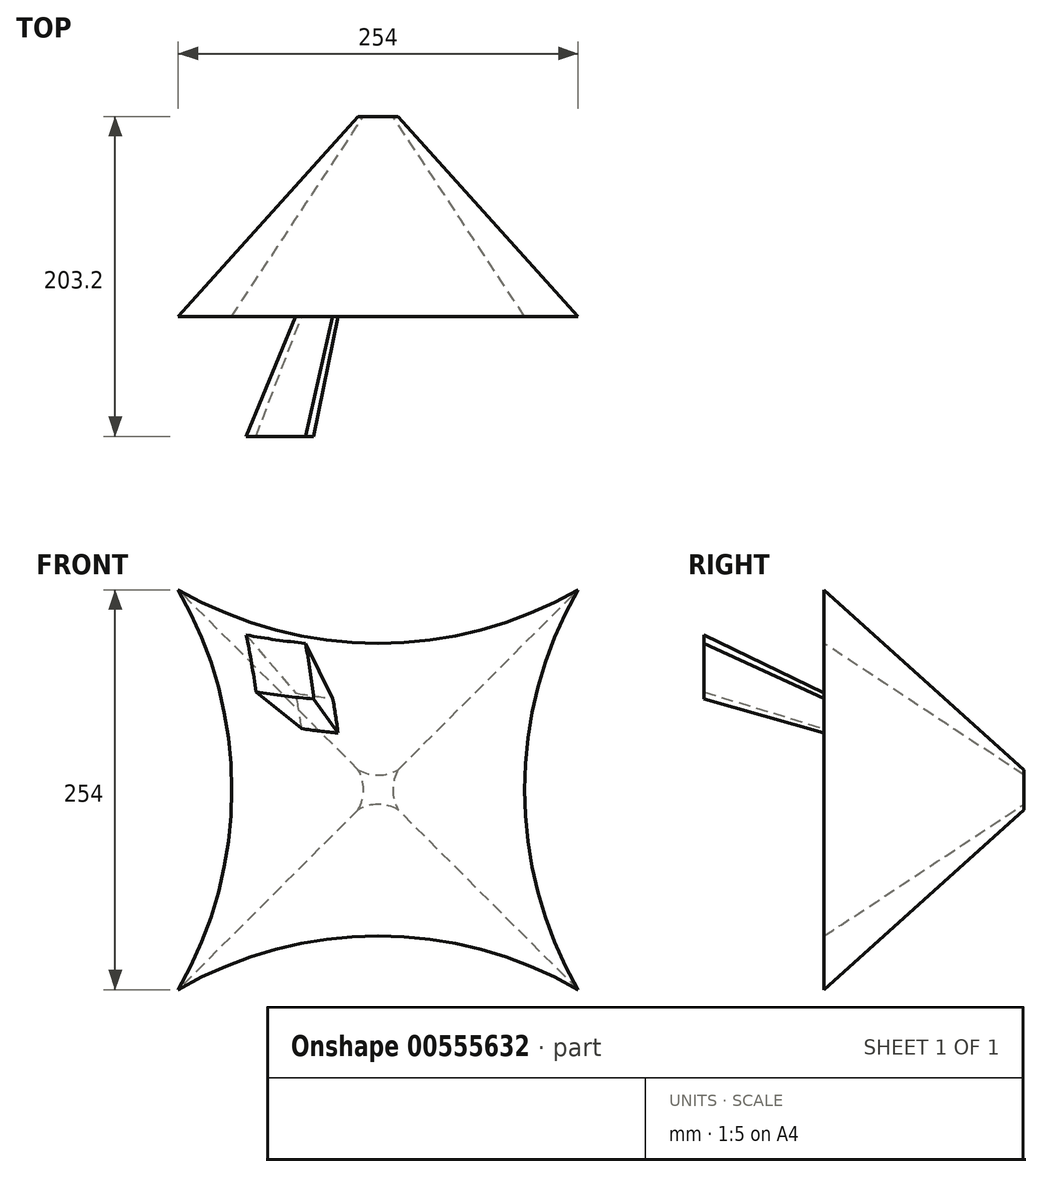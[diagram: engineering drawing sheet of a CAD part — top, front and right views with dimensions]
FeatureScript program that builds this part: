
annotation { "Feature Type Name" : "Feature", "Feature Type Description" : "" }
export const myFeature = defineFeature(function(context is Context, id is Id, definition is map)
    precondition{}
    {
        {
            var Q0;
            Q0=qCreatedBy(makeId("Front.planeOp"),FACE);
            var sketch = newSketch(context, id + "F0", { "sketchPlane" : qUnion([Q0])});
            skLineSegment(sketch, "E0.bottom", {"start": v(12.7, 12.7) * mm, "end": v(-12.7, 12.7) * mm, "construction": true});
            skLineSegment(sketch, "E0.top", {"start": v(12.7, -12.7) * mm, "end": v(-12.7, -12.7) * mm, "construction": true});
            skLineSegment(sketch, "E0.left", {"start": v(12.7, 12.7) * mm, "end": v(12.7, -12.7) * mm, "construction": true});
            skLineSegment(sketch, "E0.right", {"start": v(-12.7, 12.7) * mm, "end": v(-12.7, -12.7) * mm, "construction": true});
            skPoint(sketch, "E0.middle", {"position": v(0, 0) * mm});
            skArc(sketch, "E1", {"start": v(-12.7, 12.7) * mm, "mid": v(0, 9.3) * mm, "end": v(12.7, 12.7) * mm});
            skArc(sketch, "E2", {"start": v(12.7, 12.7) * mm, "mid": v(9.3, 0) * mm, "end": v(12.7, -12.7) * mm});
            skArc(sketch, "E3", {"start": v(12.7, -12.7) * mm, "mid": v(0, -9.3) * mm, "end": v(-12.7, -12.7) * mm});
            skArc(sketch, "E4", {"start": v(-12.7, -12.7) * mm, "mid": v(-9.3, 0) * mm, "end": v(-12.7, 12.7) * mm});
            skArc(sketch, "E5", {"start": v(-6.35, -10.1) * mm, "mid": v(-4.6, 0) * mm, "end": v(-6.35, 10.1) * mm});
            skArc(sketch, "E6", {"start": v(-3.8, 9.58) * mm, "mid": v(-2.36, 0) * mm, "end": v(-3.8, -9.58) * mm});
            skArc(sketch, "E7", {"start": v(-10.47, 7.62) * mm, "mid": v(0, 5.67) * mm, "end": v(10.47, 7.62) * mm});
            skArc(sketch, "E8", {"start": v(-9.81, 5.08) * mm, "mid": v(0, 3.5) * mm, "end": v(9.81, 5.08) * mm});
            skSolve(sketch);
        }
        {
            var Q0;
            {var subQ0=sQuery(id+"F0.wireOp",EDGE,"E3");var subQ1=sQuery(id+"F0.wireOp",EDGE,"E2");var subQ2=makeQuery(id+"F0.imprint","INTERSECT",VERTEX,{"derivedFrom":[subQ1,subQ0]});Q0=makeQuery(id+"F0.imprint","IMPRINT",FACE,{"disambiguationData":[TD([[makeQuery(id+"F0.imprint","IMPRINT",EDGE,{"disambiguationData":[TD([[subQ2,1.0]])],"derivedFrom":subQ1}),-1.0]])]});}
            var sketch = newSketch(context, id + "F1", { "sketchPlane" : qUnion([Q0])});
            skArc(sketch, "E9.0", {"start": v(-12.7, -12.7) * mm, "mid": v(-9.3, 0) * mm, "end": v(-12.7, 12.7) * mm});
            skArc(sketch, "E9.1", {"start": v(12.7, -12.7) * mm, "mid": v(0, -9.3) * mm, "end": v(-12.7, -12.7) * mm});
            skArc(sketch, "E9.2", {"start": v(12.7, 12.7) * mm, "mid": v(9.3, 0) * mm, "end": v(12.7, -12.7) * mm});
            skArc(sketch, "E9.3", {"start": v(-12.7, 12.7) * mm, "mid": v(0, 9.3) * mm, "end": v(12.7, 12.7) * mm});
            skSolve(sketch);
        }
        {
            var Q0;
            Q0=qCreatedBy(makeId("Front.planeOp"),FACE);
            cPlane(context, id + "F2", {"entities" : qUnion([Q0]), "cplaneType" : CPlaneType.OFFSET, "offset" : 127 * mm, "width" : 152.4 * mm, "height" : 152.4 * mm});
        }
        {
            var Q0;
            Q0=qCreatedBy(id+"F2.planeOp",FACE);
            var sketch = newSketch(context, id + "F3", { "sketchPlane" : qUnion([Q0])});
            skLineSegment(sketch, "E10.bottom", {"start": v(127, 127) * mm, "end": v(-127, 127) * mm, "construction": true});
            skLineSegment(sketch, "E10.top", {"start": v(127, -127) * mm, "end": v(-127, -127) * mm, "construction": true});
            skLineSegment(sketch, "E10.left", {"start": v(127, 127) * mm, "end": v(127, -127) * mm, "construction": true});
            skLineSegment(sketch, "E10.right", {"start": v(-127, 127) * mm, "end": v(-127, -127) * mm, "construction": true});
            skPoint(sketch, "E10.middle", {"position": v(0, 0) * mm});
            skArc(sketch, "E11", {"start": v(-127, 127) * mm, "mid": v(0, 92.97) * mm, "end": v(127, 127) * mm});
            skArc(sketch, "E12", {"start": v(127, 127) * mm, "mid": v(92.97, 0) * mm, "end": v(127, -127) * mm});
            skArc(sketch, "E13", {"start": v(127, -127) * mm, "mid": v(0, -92.97) * mm, "end": v(-127, -127) * mm});
            skArc(sketch, "E14", {"start": v(-127, -127) * mm, "mid": v(-92.97, 0) * mm, "end": v(-127, 127) * mm});
            skArc(sketch, "E15", {"start": v(-63.5, -101.04) * mm, "mid": v(-46.03, 0) * mm, "end": v(-63.5, 101.04) * mm});
            skArc(sketch, "E16", {"start": v(-38.1, 95.84) * mm, "mid": v(-23.57, 0) * mm, "end": v(-38.1, -95.84) * mm});
            skArc(sketch, "E17", {"start": v(-104.67, 76.2) * mm, "mid": v(0, 56.67) * mm, "end": v(104.67, 76.2) * mm});
            skArc(sketch, "E18", {"start": v(-98.1, 50.8) * mm, "mid": v(0, 34.98) * mm, "end": v(98.1, 50.8) * mm});
            skSolve(sketch);
        }
        {
            var Q0;
            Q0=qCreatedBy(id+"F2.planeOp",FACE);
            var sketch = newSketch(context, id + "F4", { "sketchPlane" : qUnion([Q0])});
            skArc(sketch, "E19.0", {"start": v(-127, 127) * mm, "mid": v(0, 92.97) * mm, "end": v(127, 127) * mm});
            skArc(sketch, "E19.1", {"start": v(-127, -127) * mm, "mid": v(-92.97, 0) * mm, "end": v(-127, 127) * mm});
            skArc(sketch, "E19.2", {"start": v(127, -127) * mm, "mid": v(0, -92.97) * mm, "end": v(-127, -127) * mm});
            skArc(sketch, "E19.3", {"start": v(127, 127) * mm, "mid": v(92.97, 0) * mm, "end": v(127, -127) * mm});
            skSolve(sketch);
        }
        {
            var Q0;
            Q0=qCreatedBy(id+"F2.planeOp",FACE);
            cPlane(context, id + "F5", {"entities" : qUnion([Q0]), "cplaneType" : CPlaneType.OFFSET, "offset" : 76.2 * mm, "width" : 152.4 * mm, "height" : 152.4 * mm});
        }
        {
            var Q0;
            Q0=qCreatedBy(id+"F5.planeOp",FACE);
            var sketch = newSketch(context, id + "F6", { "sketchPlane" : qUnion([Q0])});
            skLineSegment(sketch, "E20.bottom", {"start": v(203.2, 203.2) * mm, "end": v(-203.2, 203.2) * mm, "construction": true});
            skLineSegment(sketch, "E20.top", {"start": v(203.2, -203.2) * mm, "end": v(-203.2, -203.2) * mm, "construction": true});
            skLineSegment(sketch, "E20.left", {"start": v(203.2, 203.2) * mm, "end": v(203.2, -203.2) * mm, "construction": true});
            skLineSegment(sketch, "E20.right", {"start": v(-203.2, 203.2) * mm, "end": v(-203.2, -203.2) * mm, "construction": true});
            skPoint(sketch, "E20.middle", {"position": v(0, 0) * mm});
            skArc(sketch, "E21", {"start": v(-203.2, 203.2) * mm, "mid": v(0, 148.75) * mm, "end": v(203.2, 203.2) * mm});
            skArc(sketch, "E22", {"start": v(203.2, 203.2) * mm, "mid": v(148.75, 0) * mm, "end": v(203.2, -203.2) * mm});
            skArc(sketch, "E23", {"start": v(203.2, -203.2) * mm, "mid": v(0, -148.75) * mm, "end": v(-203.2, -203.2) * mm});
            skArc(sketch, "E24", {"start": v(-203.2, -203.2) * mm, "mid": v(-148.75, 0) * mm, "end": v(-203.2, 203.2) * mm});
            skArc(sketch, "E25", {"start": v(-101.6, -161.66) * mm, "mid": v(-73.65, 0) * mm, "end": v(-101.6, 161.66) * mm});
            skArc(sketch, "E26", {"start": v(-60.96, 153.35) * mm, "mid": v(-37.71, 0) * mm, "end": v(-60.96, -153.35) * mm});
            skArc(sketch, "E27", {"start": v(-167.47, 121.92) * mm, "mid": v(0, 90.68) * mm, "end": v(167.47, 121.92) * mm});
            skArc(sketch, "E28", {"start": v(-156.96, 81.28) * mm, "mid": v(0, 55.96) * mm, "end": v(156.96, 81.28) * mm});
            skSolve(sketch);
        }
        {
            var Q0;
            Q0=sQuery(id+"F0.wireOp",VERTEX,"E0.bottom.start");
            var Q1;
            Q1=sQuery(id+"F0.wireOp",VERTEX,"E3.start");
            var Q2;
            Q2=sQuery(id+"F4.wireOp",VERTEX,"E19.3.end");
            cPlane(context, id + "F7", {"entities" : qUnion([Q0, Q1, Q2]), "cplaneType" : CPlaneType.THREE_POINT, "offset" : 25.4 * mm, "width" : 152.4 * mm, "height" : 152.4 * mm});
        }
        {
            var Q0;
            Q0=qCreatedBy(id+"F7.planeOp",FACE);
            var sketch = newSketch(context, id + "F8", { "sketchPlane" : qUnion([Q0])});
            skLineSegment(sketch, "E29", {"start": v(-179.36, -127) * mm, "end": v(-8.5, -12.7) * mm});
            skLineSegment(sketch, "E30", {"start": v(-8.5, 12.7) * mm, "end": v(-179.36, 127) * mm});
            skSolve(sketch);
        }
        {
            var Q0;
            Q0 = qSketchRegion(id + "F1", true);
            var Q1;
            Q1 = qSketchRegion(id + "F4", true);
            var Q2;
            Q2=sQuery(id+"F8.wireOp",EDGE,"E30");
            var Q3;
            Q3=sQuery(id+"F8.wireOp",EDGE,"E29");
            var Q4;
            Q4=sQuery(id+"F0.wireOp",VERTEX,"E0.right.end");
            var Q5;
            Q5=sQuery(id+"F3.wireOp",VERTEX,"E10.top.end");
            loft(context, id + "F9", {"addGuides" : true, "sheetProfilesArray" : [{ "sheetProfileEntities" : qUnion([Q0]) }, { "sheetProfileEntities" : qUnion([Q1]) }], "guidesArray" : [{ "guideEntities" : qUnion([Q2]), "guideDerivativeType" : LoftGuideDerivativeType.DEFAULT, "guideDerivativeMagnitude" : 1 }, { "guideEntities" : qUnion([Q3]), "guideDerivativeType" : LoftGuideDerivativeType.DEFAULT, "guideDerivativeMagnitude" : 1 }], "matchConnections" : true, "connections" : [{ "connectionEntities" : qUnion([Q4, Q5]), "connectionEdgeQueries" : qUnion([]), "connectionEdgeParameters" : [] }]});
        }
        {
            var Q1;
            {var subQ0=sQuery(id+"F6.wireOp",EDGE,"E28");var subQ1=sQuery(id+"F6.wireOp",EDGE,"E25");var subQ2=makeQuery(id+"F6.imprint","INTERSECT",VERTEX,{"derivedFrom":[subQ1,subQ0]});Q1=makeQuery(id+"F6.imprint","IMPRINT",FACE,{"disambiguationData":[TD([[makeQuery(id+"F6.imprint","IMPRINT",EDGE,{"disambiguationData":[TD([[subQ2,-1.0]])],"derivedFrom":subQ1}),-1.0]])]});}
            var Q2;
            {var subQ0=sQuery(id+"F3.wireOp",EDGE,"E18");var subQ1=sQuery(id+"F3.wireOp",EDGE,"E15");var subQ2=makeQuery(id+"F3.imprint","INTERSECT",VERTEX,{"derivedFrom":[subQ1,subQ0]});Q2=makeQuery(id+"F3.imprint","IMPRINT",FACE,{"disambiguationData":[TD([[makeQuery(id+"F3.imprint","IMPRINT",EDGE,{"disambiguationData":[TD([[subQ2,-1.0]])],"derivedFrom":subQ1}),-1.0]])]});}
            loft(context, id + "F10", {"operationType" : NewBodyOperationType.ADD, "sheetProfilesArray" : [{ "sheetProfileEntities" : qUnion([Q1]) }, { "sheetProfileEntities" : qUnion([Q2]) }]});
        }
    });
